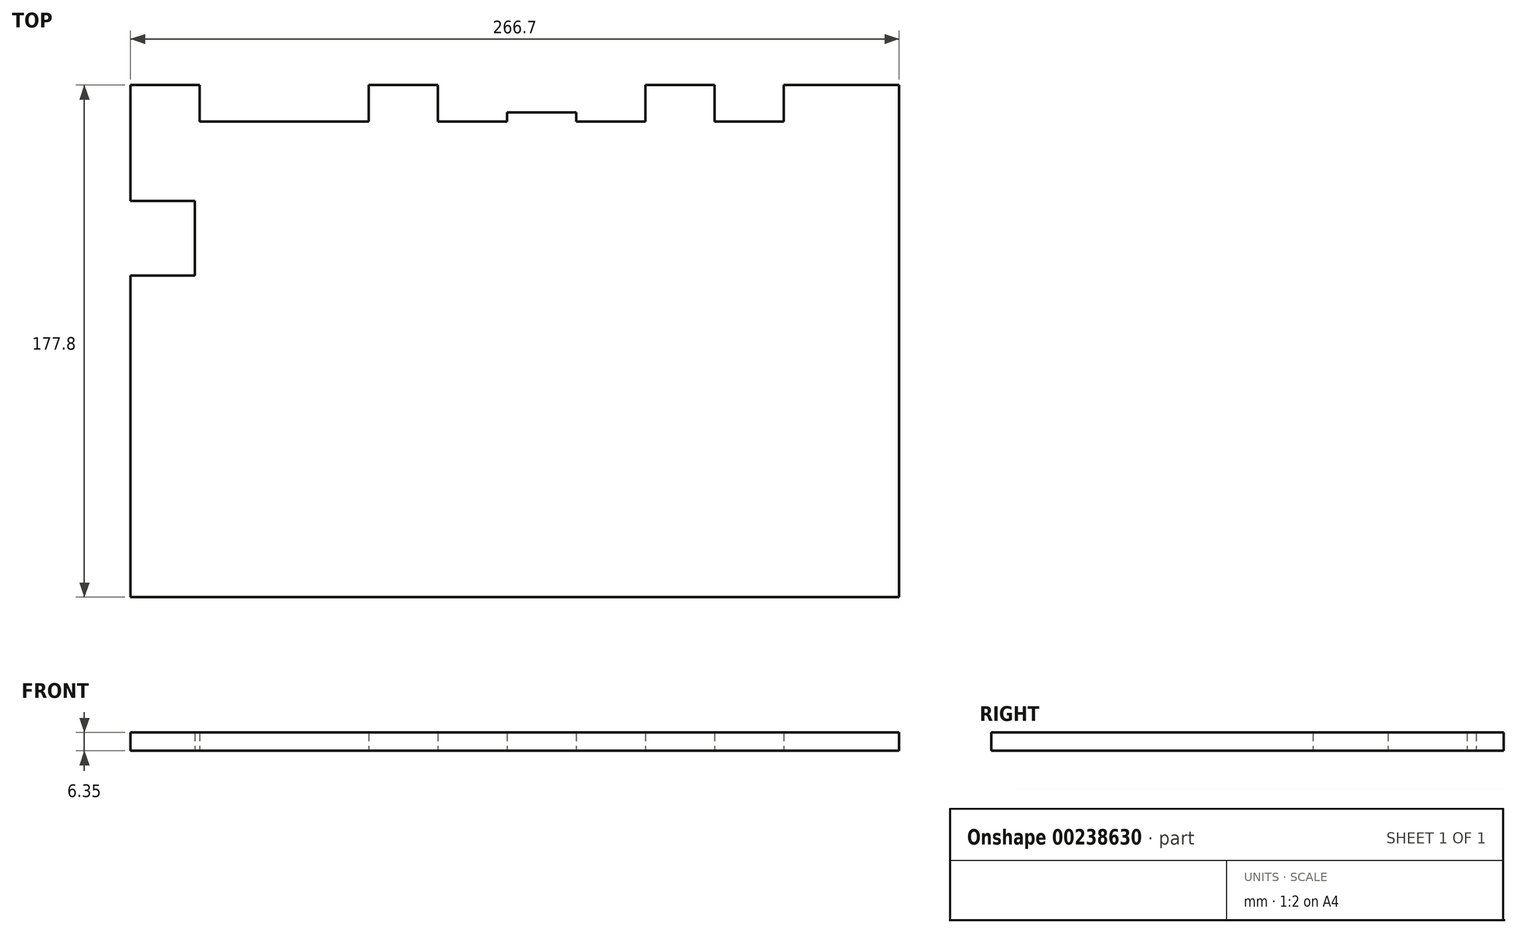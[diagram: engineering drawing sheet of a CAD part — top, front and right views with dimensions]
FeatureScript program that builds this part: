
annotation { "Feature Type Name" : "Feature", "Feature Type Description" : "" }
export const myFeature = defineFeature(function(context is Context, id is Id, definition is map)
    precondition{}
    {
        {
            var Q0;
            Q0=qCreatedBy(makeId("Top.planeOp"),FACE);
            var sketch = newSketch(context, id + "F0", { "sketchPlane" : qUnion([Q0])});
            skLineSegment(sketch, "E0.bottom", {"start": v(0, 0) * mm, "end": v(266.7, 0) * mm});
            skLineSegment(sketch, "E0.top", {"start": v(0, 177.8) * mm, "end": v(24, 177.8) * mm});
            skLineSegment(sketch, "E0.left", {"start": v(0, 0) * mm, "end": v(0, 111.66) * mm});
            skLineSegment(sketch, "E0.right", {"start": v(266.7, 0) * mm, "end": v(266.7, 177.8) * mm});
            skLineSegment(sketch, "E1", {"start": v(24, 177.8) * mm, "end": v(24, 165.1) * mm});
            skLineSegment(sketch, "E2", {"start": v(24, 165.1) * mm, "end": v(82.67, 165.1) * mm});
            skLineSegment(sketch, "E3", {"start": v(82.67, 165.1) * mm, "end": v(82.67, 177.8) * mm});
            skLineSegment(sketch, "E4.trimOffspring", {"start": v(82.67, 177.8) * mm, "end": v(106.67, 177.8) * mm});
            skLineSegment(sketch, "E5", {"start": v(0, 137.6) * mm, "end": v(22.32, 137.6) * mm});
            skLineSegment(sketch, "E6", {"start": v(22.32, 137.6) * mm, "end": v(22.32, 111.66) * mm});
            skLineSegment(sketch, "E7", {"start": v(22.32, 111.66) * mm, "end": v(0, 111.66) * mm});
            skLineSegment(sketch, "E8.trimOffspring", {"start": v(0, 137.6) * mm, "end": v(0, 177.8) * mm});
            skLineSegment(sketch, "E9", {"start": v(106.67, 177.8) * mm, "end": v(106.67, 165.1) * mm});
            skLineSegment(sketch, "E10", {"start": v(130.67, 165.1) * mm, "end": v(106.67, 165.1) * mm});
            skLineSegment(sketch, "E11", {"start": v(130.67, 165.1) * mm, "end": v(130.67, 168.28) * mm});
            skLineSegment(sketch, "E12", {"start": v(154.67, 168.28) * mm, "end": v(154.67, 165.1) * mm});
            skLineSegment(sketch, "E13", {"start": v(154.67, 165.1) * mm, "end": v(178.67, 165.1) * mm});
            skLineSegment(sketch, "E14", {"start": v(178.67, 165.1) * mm, "end": v(178.67, 177.8) * mm});
            skLineSegment(sketch, "E15", {"start": v(130.67, 168.27) * mm, "end": v(154.67, 168.28) * mm});
            skLineSegment(sketch, "E16", {"start": v(178.67, 177.8) * mm, "end": v(202.67, 177.8) * mm});
            skLineSegment(sketch, "E17", {"start": v(202.67, 177.8) * mm, "end": v(202.67, 165.1) * mm});
            skLineSegment(sketch, "E18", {"start": v(202.67, 165.1) * mm, "end": v(226.67, 165.1) * mm});
            skLineSegment(sketch, "E19", {"start": v(226.67, 165.1) * mm, "end": v(226.67, 177.8) * mm});
            skLineSegment(sketch, "E20.trimOffspring", {"start": v(226.67, 177.8) * mm, "end": v(266.7, 177.8) * mm});
            skSolve(sketch);
        }
        {
            var Q0;
            Q0=makeQuery(id+"F0.imprint","IMPRINT",FACE,{"disambiguationData":[TD([[makeQuery(id+"F0.imprint","IMPRINT",EDGE,{"derivedFrom":sQuery(id+"F0.wireOp",EDGE,"E0.bottom")}),1.0]])]});
            extrude(context, id + "F1", {"entities" : qUnion([Q0]), "depth" : 6.35 * mm});
        }
    });
